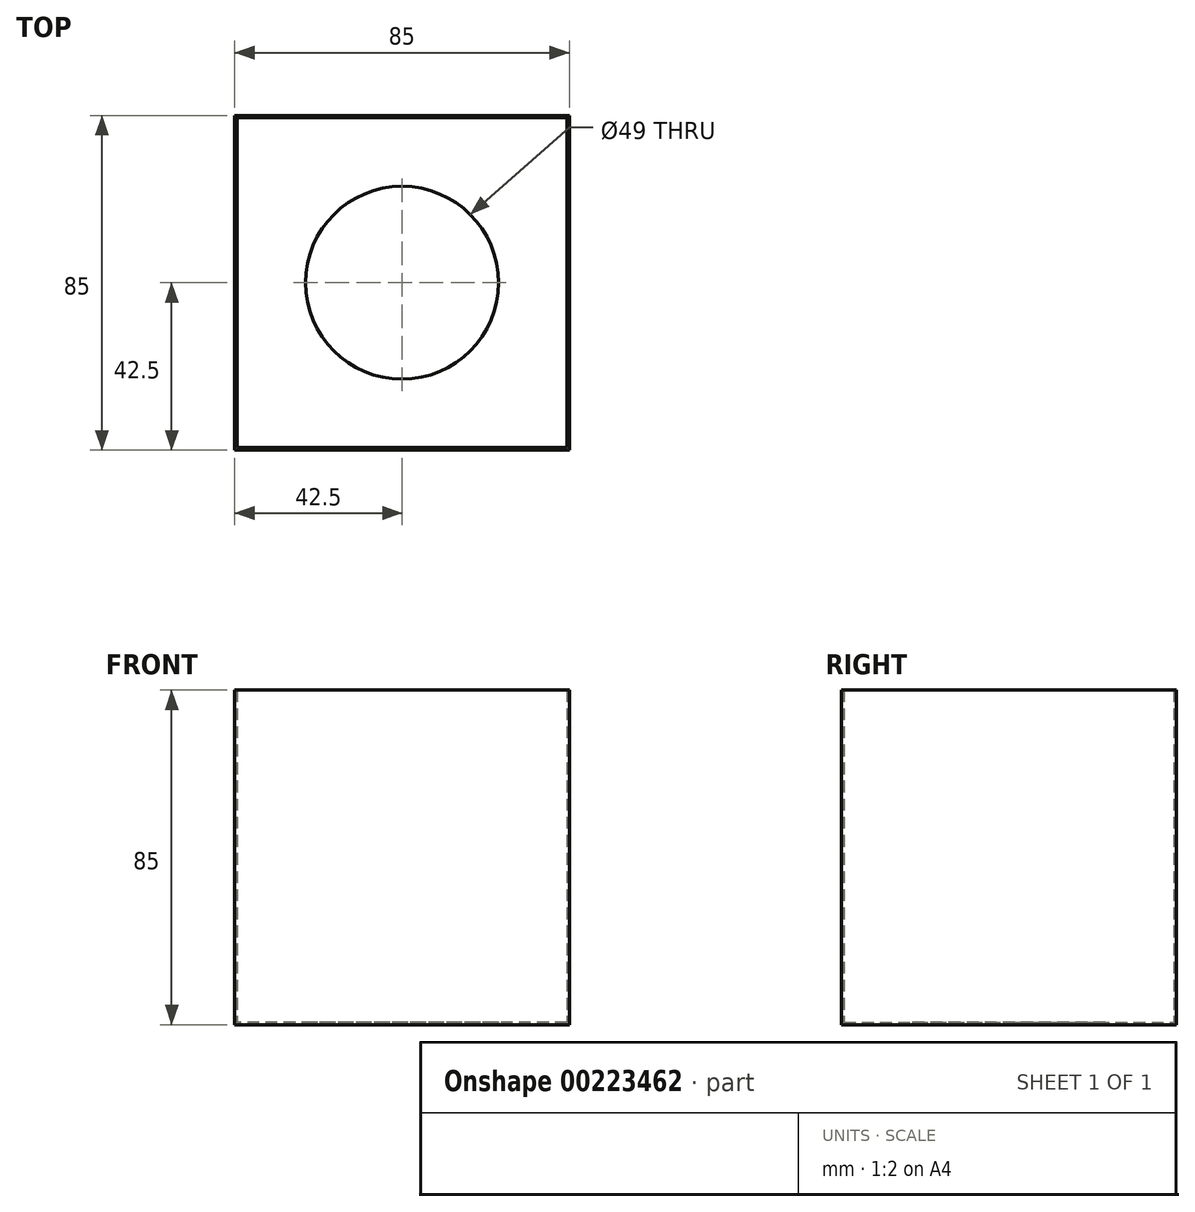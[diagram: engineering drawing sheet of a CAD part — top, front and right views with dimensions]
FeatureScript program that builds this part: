
annotation { "Feature Type Name" : "Feature", "Feature Type Description" : "" }
export const myFeature = defineFeature(function(context is Context, id is Id, definition is map)
    precondition{}
    {
        {
            var Q0;
            Q0=qCreatedBy(makeId("Top.planeOp"),FACE);
            var sketch = newSketch(context, id + "F0", { "sketchPlane" : qUnion([Q0])});
            skLineSegment(sketch, "E0.bottom", {"start": v(42.5, -42.5) * mm, "end": v(-42.5, -42.5) * mm});
            skLineSegment(sketch, "E0.top", {"start": v(42.5, 42.5) * mm, "end": v(-42.5, 42.5) * mm});
            skLineSegment(sketch, "E0.left", {"start": v(42.5, -42.5) * mm, "end": v(42.5, 42.5) * mm});
            skLineSegment(sketch, "E0.right", {"start": v(-42.5, -42.5) * mm, "end": v(-42.5, 42.5) * mm});
            skPoint(sketch, "E0.middle", {"position": v(0, 0) * mm});
            skSolve(sketch);
        }
        {
            var Q0;
            Q0=makeQuery(id+"F0.imprint","IMPRINT",FACE,{"disambiguationData":[TD([[makeQuery(id+"F0.imprint","IMPRINT",EDGE,{"derivedFrom":sQuery(id+"F0.wireOp",EDGE,"E0.bottom")}),-1.0]])]});
            extrude(context, id + "F1", {"entities" : qUnion([Q0]), "depth" : 85 * mm});
        }
        {
            var Q0;
            Q0=makeQuery(id+"F1.opExtrude","CAP_FACE",FACE,{"disambiguationData":[OSD([sQuery(id+"F0.wireOp",EDGE,"E0.bottom"),sQuery(id+"F0.wireOp",EDGE,"E0.top"),sQuery(id+"F0.wireOp",EDGE,"E0.left"),sQuery(id+"F0.wireOp",EDGE,"E0.right")])],"isStart":false});
            shell(context, id + "F2", {"entities" : qUnion([Q0]), "thickness" : 0.6 * mm});
        }
        {
            var Q0;
            Q0=qCreatedBy(makeId("Top.planeOp"),FACE);
            var sketch = newSketch(context, id + "F3", { "sketchPlane" : qUnion([Q0])});
            skCircle(sketch, "E1", {"center": v(0, 0) * mm, "radius": 24.5 * mm});
            skSolve(sketch);
        }
        {
            var Q0;
            Q0 = qSketchRegion(id + "F3", true);
            extrude(context, id + "F4", {"entities" : qUnion([Q0]), "operationType" : NewBodyOperationType.REMOVE, "depth" : 25 * mm});
        }
    });
